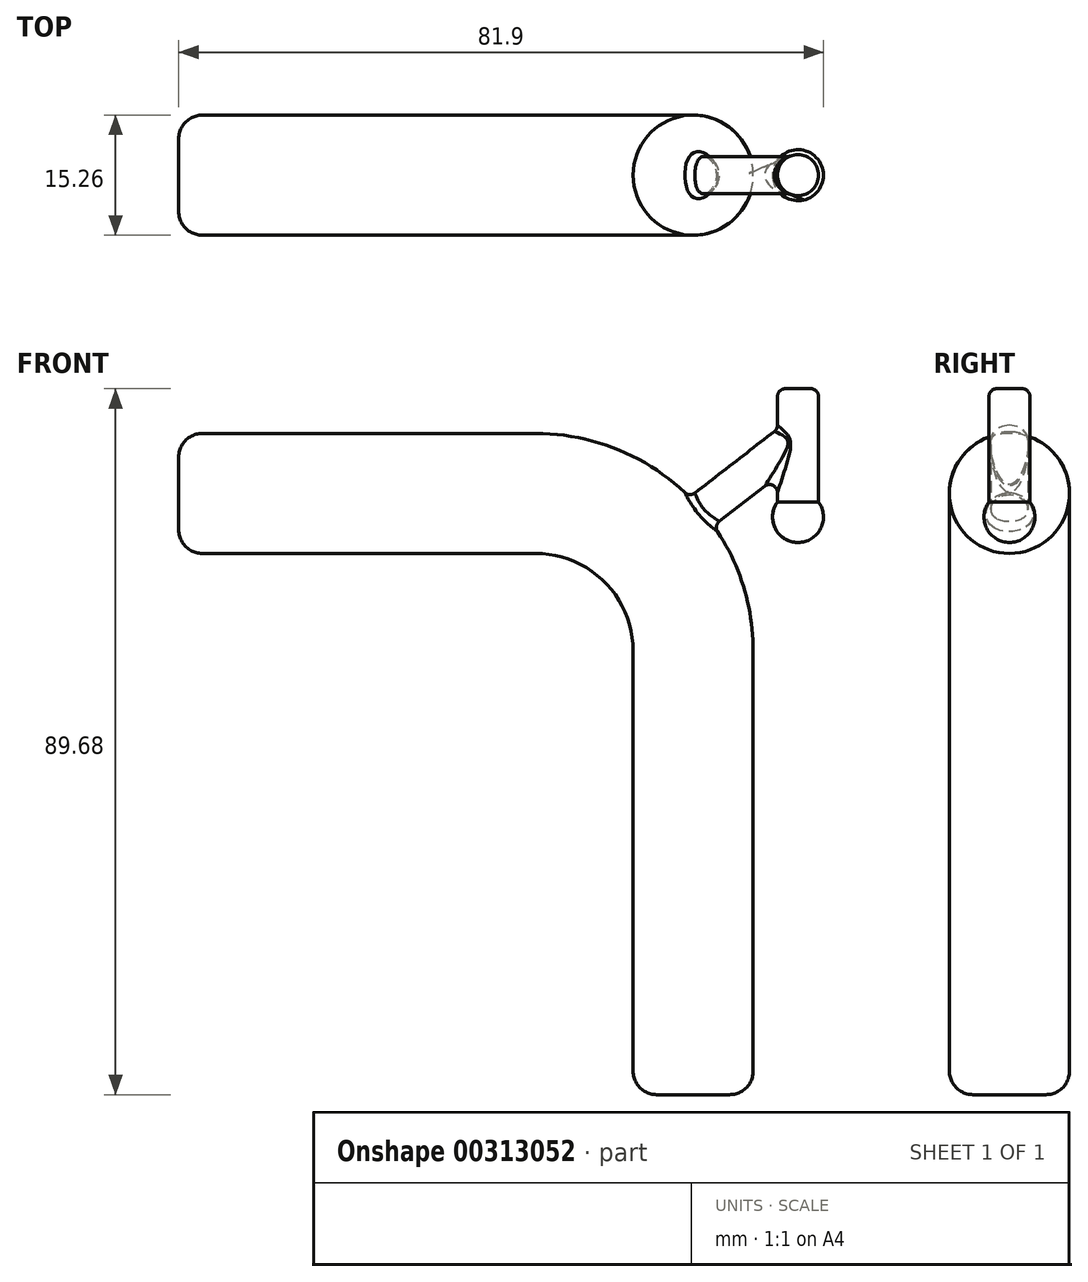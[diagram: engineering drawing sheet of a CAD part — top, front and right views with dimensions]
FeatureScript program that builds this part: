
annotation { "Feature Type Name" : "Feature", "Feature Type Description" : "" }
export const myFeature = defineFeature(function(context is Context, id is Id, definition is map)
    precondition{}
    {
        {
            var Q0;
            Q0=qCreatedBy(makeId("Front.planeOp"),FACE);
            var sketch = newSketch(context, id + "F0", { "sketchPlane" : qUnion([Q0])});
            skLineSegment(sketch, "E0", {"start": v(0, 0) * mm, "end": v(45.35, 0) * mm});
            skLineSegment(sketch, "E1", {"start": v(65.35, -20) * mm, "end": v(65.35, -76.38) * mm});
            skPoint(sketch, "E2.visualSharp", {"position": v(65.35, 0) * mm});
            skArc(sketch, "E2.filletArc", {"start": v(65.35, -20) * mm, "mid": v(59.5, -5.86) * mm, "end": v(45.35, 0) * mm});
            skSolve(sketch);
        }
        {
            var Q0;
            Q0=qCreatedBy(makeId("Right.planeOp"),FACE);
            var sketch = newSketch(context, id + "F1", { "sketchPlane" : qUnion([Q0])});
            skCircle(sketch, "E3", {"center": v(0, 0) * mm, "radius": 7.63 * mm});
            skSolve(sketch);
        }
        {
            var Q0;
            Q0=makeQuery(id+"F1.imprint","IMPRINT",FACE,{"disambiguationData":[TD([[makeQuery(id+"F1.imprint","IMPRINT",EDGE,{"derivedFrom":sQuery(id+"F1.wireOp",EDGE,"E3")}),1.0]])]});
            var Q1;
            Q1=sQuery(id+"F0.wireOp",EDGE,"E2.filletArc");
            var Q2;
            Q2=sQuery(id+"F0.wireOp",EDGE,"E0");
            var Q3;
            Q3=sQuery(id+"F0.wireOp",EDGE,"E1");
            sweep(context, id + "F2", {"profiles" : qUnion([Q0]), "path" : qUnion([Q1, Q2, Q3])});
        }
        {
            var Q0;
            Q0=qCreatedBy(makeId("Front.planeOp"),FACE);
            var sketch = newSketch(context, id + "F3", { "sketchPlane" : qUnion([Q0])});
            skLineSegment(sketch, "E4", {"start": v(64.86, -3.5) * mm, "end": v(78.73, 7.25) * mm});
            skLineSegment(sketch, "E5", {"start": v(78.73, 7.25) * mm, "end": v(80.18, 5.37) * mm});
            skLineSegment(sketch, "E6", {"start": v(80.18, 5.37) * mm, "end": v(66.27, -5.41) * mm});
            skLineSegment(sketch, "E7", {"start": v(66.27, -5.41) * mm, "end": v(64.86, -3.5) * mm});
            skSolve(sketch);
        }
        {
            var Q0;
            Q0=makeQuery(id+"F3.imprint","IMPRINT",FACE,{"disambiguationData":[TD([[makeQuery(id+"F3.imprint","IMPRINT",EDGE,{"derivedFrom":sQuery(id+"F3.wireOp",EDGE,"E4")}),-1.0]])]});
            var Q1;
            Q1=sQuery(id+"F3.wireOp",EDGE,"E4");
            revolve(context, id + "F4", {"operationType" : NewBodyOperationType.ADD, "entities" : qUnion([Q0]), "axis" : qUnion([Q1]), "revolveType" : RevolveType.FULL});
        }
        {
            var Q0;
            Q0=qCreatedBy(makeId("Front.planeOp"),FACE);
            var sketch = newSketch(context, id + "F5", { "sketchPlane" : qUnion([Q0])});
            skLineSegment(sketch, "E8", {"start": v(78.67, 13.3) * mm, "end": v(78.67, -3) * mm});
            skLineSegment(sketch, "E9", {"start": v(78.67, -3) * mm, "end": v(81.28, -3) * mm});
            skLineSegment(sketch, "E10", {"start": v(81.28, -3) * mm, "end": v(81.28, 13.3) * mm});
            skLineSegment(sketch, "E11", {"start": v(81.28, 13.3) * mm, "end": v(78.67, 13.3) * mm});
            skArc(sketch, "E12", {"start": v(78.67, -6.23) * mm, "mid": v(80.95, -5.28) * mm, "end": v(81.9, -3) * mm});
            skLineSegment(sketch, "E13", {"start": v(78.67, -3) * mm, "end": v(78.67, -6.23) * mm});
            skLineSegment(sketch, "E14", {"start": v(81.28, -3) * mm, "end": v(81.9, -3) * mm});
            skArc(sketch, "E15", {"start": v(81.9, -3) * mm, "mid": v(81.74, -2) * mm, "end": v(81.28, -1.09) * mm});
            skSolve(sketch);
        }
        {
            var Q0;
            Q0=makeQuery(id+"F5.imprint","IMPRINT",FACE,{"disambiguationData":[TD([[makeQuery(id+"F5.imprint","IMPRINT",EDGE,{"derivedFrom":sQuery(id+"F5.wireOp",EDGE,"E8")}),1.0]])]});
            var Q1;
            Q1=makeQuery(id+"F5.imprint","IMPRINT",FACE,{"disambiguationData":[TD([[makeQuery(id+"F5.imprint","IMPRINT",EDGE,{"derivedFrom":sQuery(id+"F5.wireOp",EDGE,"E9")}),-1.0]])]});
            var Q2;
            {var subQ0=sQuery(id+"F5.wireOp",EDGE,"E14");Q2=makeQuery(id+"F5.imprint","IMPRINT",FACE,{"disambiguationData":[TD([[makeQuery(id+"F5.imprint","IMPRINT",EDGE,{"derivedFrom":subQ0}),1.0]])]});}
            var Q3;
            Q3=sQuery(id+"F5.wireOp",EDGE,"E8");
            revolve(context, id + "F6", {"operationType" : NewBodyOperationType.ADD, "entities" : qUnion([Q0, Q1, Q2]), "axis" : qUnion([Q3]), "revolveType" : RevolveType.FULL});
        }
        {
            var Q0;
            Q0=makeQuery(id+"F2.opSweep","CAP_EDGE",EDGE,{"disambiguationData":[OSD([sQuery(id+"F0.wireOp",VERTEX,"E0.start"),sQuery(id+"F1.wireOp",EDGE,"E3")])],"isStart":true});
            var Q1;
            Q1=makeQuery(id+"F2.opSweep","CAP_EDGE",EDGE,{"disambiguationData":[OSD([sQuery(id+"F0.wireOp",VERTEX,"E1.end"),sQuery(id+"F1.wireOp",EDGE,"E3")])],"isStart":false});
            fillet(context, id + "F7", {"entities" : qUnion([Q0, Q1]), "radius" : 3 * mm, "tangentPropagation" : true, "allowEdgeOverflow" : false});
        }
        {
            var Q0;
            Q0=makeQuery(id+"F6.opRevolve","SWEPT_EDGE",EDGE,{"disambiguationData":[OSD([sQuery(id+"F5.wireOp",EDGE,"E10"),sQuery(id+"F5.wireOp",EDGE,"E11")])]});
            fillet(context, id + "F8", {"entities" : qUnion([Q0]), "radius" : 1 * mm, "tangentPropagation" : true, "allowEdgeOverflow" : false});
        }
        {
            var Q0;
            Q0=makeQuery(id+"F4.boolean.opBoolean","INTERSECT",EDGE,{"derivedFrom":[makeQuery(id+"F2.opSweep","SWEPT_FACE",FACE,{"disambiguationData":[OSD([sQuery(id+"F0.wireOp",EDGE,"E2.filletArc"),sQuery(id+"F1.wireOp",EDGE,"E3")])]}),makeQuery(id+"F4.opRevolve","SWEPT_FACE",FACE,{"disambiguationData":[OSD([sQuery(id+"F3.wireOp",EDGE,"E6")])]})]});
            fillet(context, id + "F9", {"entities" : qUnion([Q0]), "radius" : 1 * mm, "allowEdgeOverflow" : false});
        }
        {
            var Q0;
            Q0=makeQuery(id+"F6.boolean.opBoolean","INTERSECT",EDGE,{"derivedFrom":[makeQuery(id+"F4.opRevolve","SWEPT_FACE",FACE,{"disambiguationData":[OSD([sQuery(id+"F3.wireOp",EDGE,"E6")])]}),makeQuery(id+"F6.opRevolve","SWEPT_FACE",FACE,{"disambiguationData":[OSD([sQuery(id+"F5.wireOp",EDGE,"E10")])]})]});
            fillet(context, id + "F10", {"entities" : qUnion([Q0]), "radius" : 1 * mm, "allowEdgeOverflow" : false});
        }
    });
